# Revit family: NBS_AndersonGECLtd_LrgMrrs_Mirror
name_source: partatom
category: Furniture
revit_build: Autodesk Revit 2017 (Build: 20160225_1515(x64)
units: mm (PartAtom-declared; Revit-internal decimal feet)

## family parameters
Cut with Voids When Loaded = No
Host = Face
Room Calculation Point = No
Shared = No

## types (1)
- Mirror
    AssetType = Fixed
    BIMObjectName = NBS_AndersonGECLtd_LargeMirrors_Mirror
    Category = Pr_25_71_53_46:Large mirrors
    CodePerformance = EN 1.4301
    Default Elevation = 1500 mm  [stored 4.92126 ft]
    Description = Stainless steel mirrors that provide a safe, alternative to glass mirror
    DurationUnit = year
    EdgesProfile = Square or rounded corners
    Features = Unbreakable, easy to clean
    Finish = Polished stainless steel
    Fixing = Adhesive or screws
    IfcExportAs = IfcFurnitureType
    IfcExportType = USERDEFINED
    IsBuiltIn = Yes
    ManufacturerName = Anderson, GEC Ltd
    ManufacturerURL = www.gecanderson.co.uk
    Material = Stainless steel
    MirrorHeight = 1200 mm  [stored 3.93701 ft]
    MirrorMaterial = NBS_Concept
    MirrorThickness = 1 mm  [stored 0.00328084 ft]
    MirrorWidth = 2400 mm
    ModelNumber = GEC Anderson stainless steel mirror
    ModelReference = Mirror
    NBSCertification = www.nationalbimlibrary.com/cert/3uur4iok
    NBSDescription = Large mirrors
    NBSReference = 45-35-55/310
    Name = LargeMirrors_Mirror_AndersonGECLtd
    NominalDepth = 1 mm  [stored 0.00328084 ft]
    NominalHeight = 1200 mm  [stored 3.93701 ft]
    NominalLength = 2400 mm
    NominalWidth = 2400 mm
    ProductInformation = http://www.gecanderson.co.uk
    Shape = Rectangle
    Size = 2400 x 1200 mm
    Status = UNSET
    Style = Mirror
    SustainabilityPerformance = 100% Recyclable
    Uniclass2015Code = Pr_25_71_53_46
    Uniclass2015Title = Large mirrors
    Uniclass2015Version = Products v1.11
    Version = 1
    WarrantyDurationUnit = year

note: [stored X ft] marks values corroborated as IEEE doubles in the binary element streams (Revit-internal decimal feet)

## geometry (parser evidence)
native form markers: Sweep x3
no freeform markers — native parametric forms only
